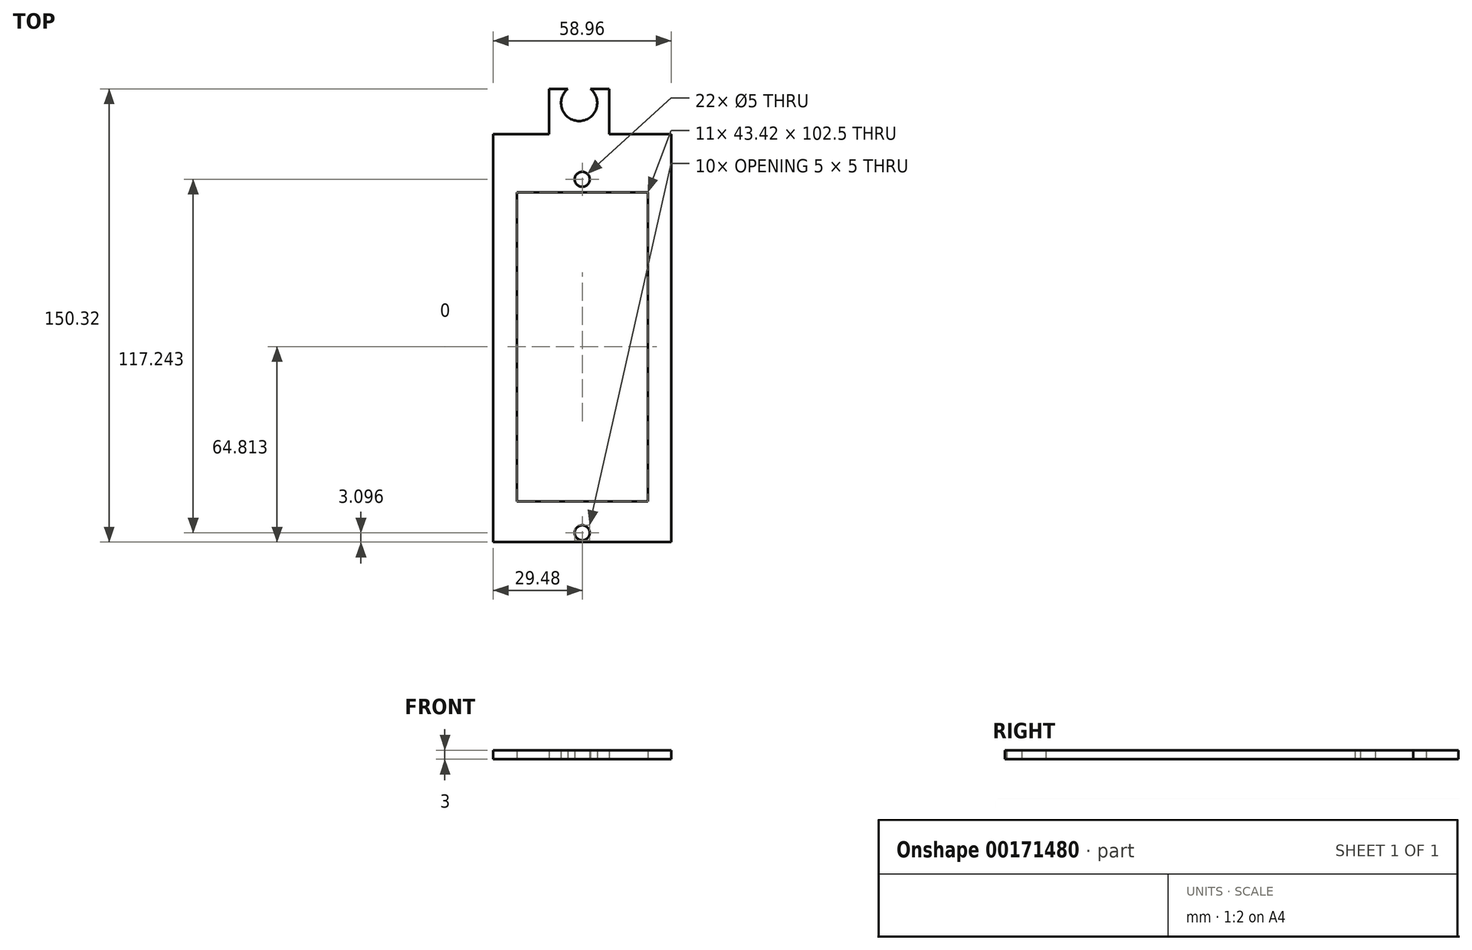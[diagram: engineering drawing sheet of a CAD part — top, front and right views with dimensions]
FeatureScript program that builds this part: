
annotation { "Feature Type Name" : "Feature", "Feature Type Description" : "" }
export const myFeature = defineFeature(function(context is Context, id is Id, definition is map)
    precondition{}
    {
        {
            var Q0;
            Q0=qCreatedBy(makeId("Top.planeOp"),FACE);
            var sketch = newSketch(context, id + "F0", { "sketchPlane" : qUnion([Q0])});
            skLineSegment(sketch, "E0.top", {"start": v(-29.48, -77.98) * mm, "end": v(29.48, -77.98) * mm});
            skLineSegment(sketch, "E0.left", {"start": v(-29.48, 57.34) * mm, "end": v(-29.48, -77.98) * mm});
            skLineSegment(sketch, "E0.right", {"start": v(29.48, 57.34) * mm, "end": v(29.48, -77.98) * mm});
            skLineSegment(sketch, "E1.top", {"start": v(-11.02, 72.34) * mm, "end": v(8.98, 72.34) * mm});
            skLineSegment(sketch, "E1.left", {"start": v(-11.02, 57.34) * mm, "end": v(-11.02, 72.34) * mm});
            skLineSegment(sketch, "E1.right", {"start": v(8.98, 57.34) * mm, "end": v(8.98, 72.34) * mm});
            skLineSegment(sketch, "E2.bottom", {"start": v(-21.71, 38.08) * mm, "end": v(21.71, 38.08) * mm});
            skLineSegment(sketch, "E2.top", {"start": v(-21.71, -64.42) * mm, "end": v(21.71, -64.42) * mm});
            skLineSegment(sketch, "E2.left", {"start": v(-21.71, 38.08) * mm, "end": v(-21.71, -64.42) * mm});
            skLineSegment(sketch, "E2.right", {"start": v(21.71, 38.08) * mm, "end": v(21.71, -64.42) * mm});
            skPoint(sketch, "E2.middle", {"position": v(0, -13.17) * mm});
            skPoint(sketch, "E3", {"position": v(-1.02, 67.67) * mm});
            skPoint(sketch, "E4", {"position": v(0, -74.88) * mm});
            skPoint(sketch, "E5", {"position": v(0, 42.36) * mm});
            skLineSegment(sketch, "E6", {"start": v(-29.48, 57.34) * mm, "end": v(-11.02, 57.34) * mm});
            skLineSegment(sketch, "E7", {"start": v(8.98, 57.34) * mm, "end": v(29.48, 57.34) * mm});
            skSolve(sketch);
        }
        {
            var Q0;
            Q0=makeQuery(id+"F0.imprint","IMPRINT",FACE,{"disambiguationData":[TD([[makeQuery(id+"F0.imprint","IMPRINT",EDGE,{"derivedFrom":sQuery(id+"F0.wireOp",EDGE,"E0.top")}),1.0]])]});
            extrude(context, id + "F1", {"entities" : qUnion([Q0]), "depth" : 3 * mm});
        }
        {
            var Q0;
            Q0=sQuery(id+"F0.wireOp",VERTEX,"E3");
            var Q1;
            Q1=makeQuery(id+"F1.opExtrude","SWEPT_BODY",BODY,{"disambiguationData":[OSD([sQuery(id+"F0.wireOp",EDGE,"E0.top"),sQuery(id+"F0.wireOp",EDGE,"E0.left"),sQuery(id+"F0.wireOp",EDGE,"E0.right"),sQuery(id+"F0.wireOp",EDGE,"E1.top"),sQuery(id+"F0.wireOp",EDGE,"E1.left"),sQuery(id+"F0.wireOp",EDGE,"E1.right"),sQuery(id+"F0.wireOp",EDGE,"E2.bottom"),sQuery(id+"F0.wireOp",EDGE,"E2.top"),sQuery(id+"F0.wireOp",EDGE,"E2.left"),sQuery(id+"F0.wireOp",EDGE,"E2.right"),sQuery(id+"F0.wireOp",EDGE,"E6"),sQuery(id+"F0.wireOp",EDGE,"E7")])]});
            hole(context, id + "F2", {"style" : HoleStyle.SIMPLE, "endStyle" : HoleEndStyle.BLIND, "oppositeDirection" : true, "holeDiameter" : 12 * mm, "holeDepth" : 50 * mm, "startFromSketch" : true, "locations" : qUnion([Q0]), "scope" : qUnion([Q1])});
        }
        {
            var Q0;
            Q0=sQuery(id+"F0.wireOp",VERTEX,"E5");
            var Q1;
            Q1=sQuery(id+"F0.wireOp",VERTEX,"E4");
            var Q2;
            Q2=makeQuery(id+"F1.opExtrude","SWEPT_BODY",BODY,{"disambiguationData":[OSD([sQuery(id+"F0.wireOp",EDGE,"E0.top"),sQuery(id+"F0.wireOp",EDGE,"E0.left"),sQuery(id+"F0.wireOp",EDGE,"E0.right"),sQuery(id+"F0.wireOp",EDGE,"E1.top"),sQuery(id+"F0.wireOp",EDGE,"E1.left"),sQuery(id+"F0.wireOp",EDGE,"E1.right"),sQuery(id+"F0.wireOp",EDGE,"E2.bottom"),sQuery(id+"F0.wireOp",EDGE,"E2.top"),sQuery(id+"F0.wireOp",EDGE,"E2.left"),sQuery(id+"F0.wireOp",EDGE,"E2.right"),sQuery(id+"F0.wireOp",EDGE,"E6"),sQuery(id+"F0.wireOp",EDGE,"E7")])]});
            hole(context, id + "F3", {"style" : HoleStyle.SIMPLE, "endStyle" : HoleEndStyle.BLIND, "oppositeDirection" : true, "holeDiameter" : 5 * mm, "holeDepth" : 50 * mm, "startFromSketch" : true, "locations" : qUnion([Q0, Q1]), "scope" : qUnion([Q2])});
        }
    });
